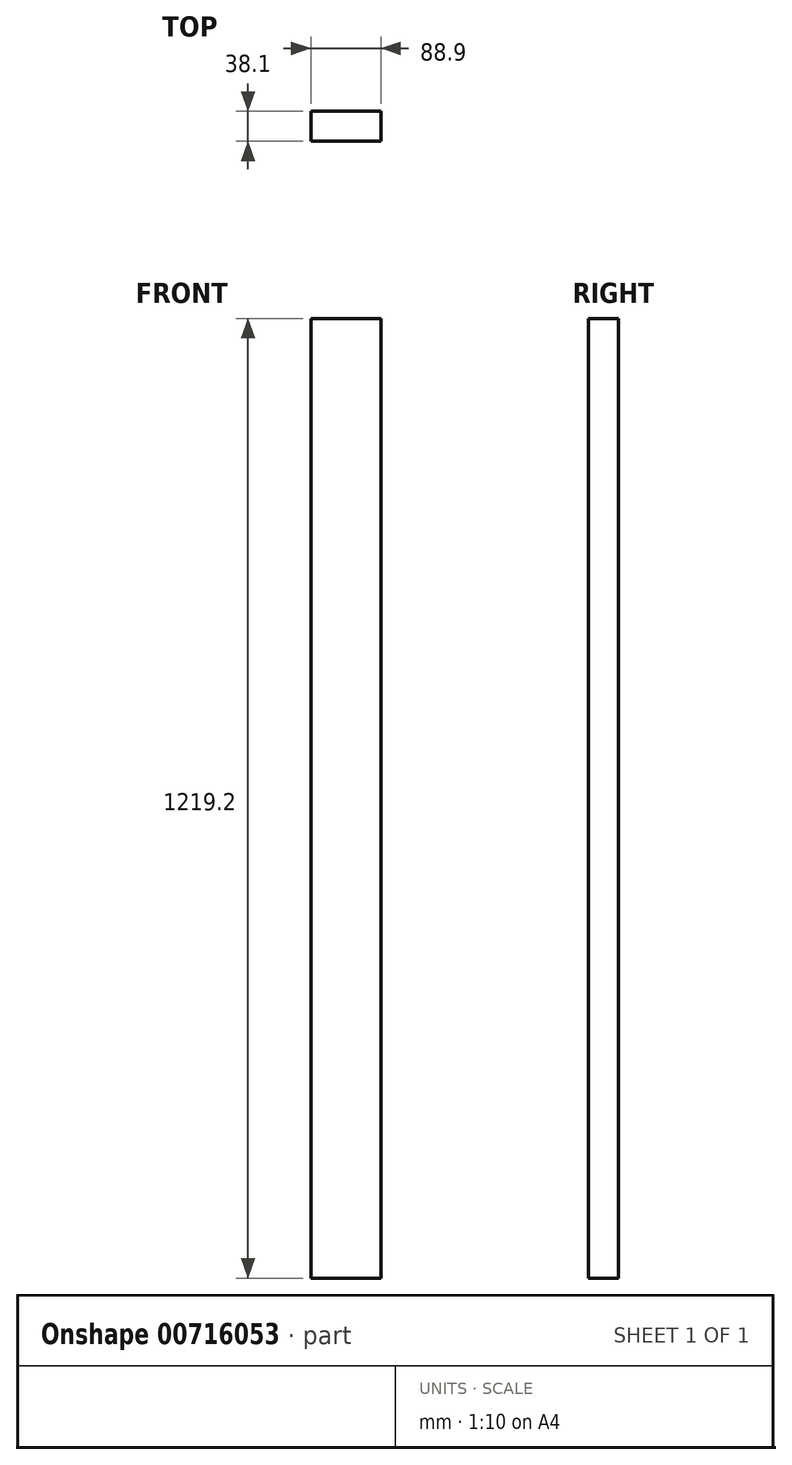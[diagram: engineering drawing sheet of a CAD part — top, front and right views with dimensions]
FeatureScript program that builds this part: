
annotation { "Feature Type Name" : "Feature", "Feature Type Description" : "" }
export const myFeature = defineFeature(function(context is Context, id is Id, definition is map)
    precondition{}
    {
        {
            var Q0;
            Q0=qCreatedBy(makeId("Top.planeOp"),FACE);
            var sketch = newSketch(context, id + "F0", { "sketchPlane" : qUnion([Q0])});
            skLineSegment(sketch, "E0.bottom", {"start": v(-44.45, 19.05) * mm, "end": v(44.45, 19.05) * mm});
            skLineSegment(sketch, "E0.top", {"start": v(-44.45, -19.05) * mm, "end": v(44.45, -19.05) * mm});
            skLineSegment(sketch, "E0.left", {"start": v(-44.45, 19.05) * mm, "end": v(-44.45, -19.05) * mm});
            skLineSegment(sketch, "E0.right", {"start": v(44.45, 19.05) * mm, "end": v(44.45, -19.05) * mm});
            skLineSegment(sketch, "E1", {"start": v(0, 0) * mm, "end": v(83.66, 0) * mm, "construction": true});
            skLineSegment(sketch, "E2", {"start": v(0, 0) * mm, "end": v(0, 50.13) * mm, "construction": true});
            skSolve(sketch);
        }
        {
            var Q0;
            Q0=makeQuery(id+"F0.imprint","IMPRINT",FACE,{"disambiguationData":[TD([[makeQuery(id+"F0.imprint","IMPRINT",EDGE,{"derivedFrom":sQuery(id+"F0.wireOp",EDGE,"E0.bottom")}),-1.0]])]});
            extrude(context, id + "F1", {"entities" : qUnion([Q0]), "depth" : -1219.2 * mm, "offsetDistance" : 25.4 * mm});
        }
    });
